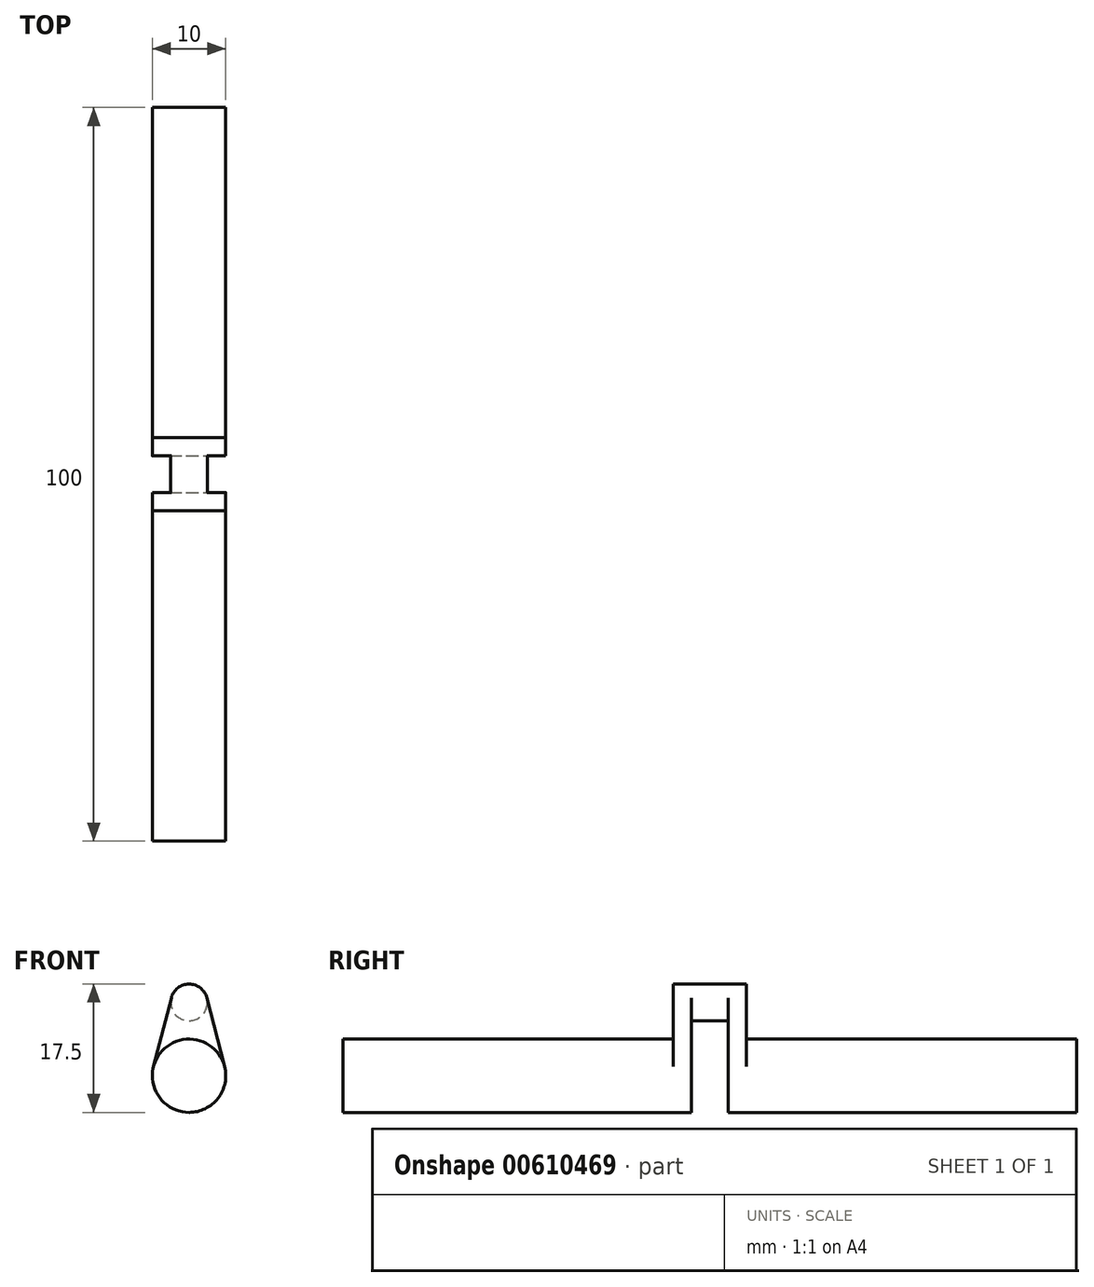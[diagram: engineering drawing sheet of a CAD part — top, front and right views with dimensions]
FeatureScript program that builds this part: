
annotation { "Feature Type Name" : "Feature", "Feature Type Description" : "" }
export const myFeature = defineFeature(function(context is Context, id is Id, definition is map)
    precondition{}
    {
        {
            var Q0;
            Q0=qCreatedBy(makeId("Front.planeOp"),FACE);
            var sketch = newSketch(context, id + "F0", { "sketchPlane" : qUnion([Q0])});
            skCircle(sketch, "E0", {"center": v(0, 0) * mm, "radius": 5 * mm});
            skLineSegment(sketch, "E1", {"start": v(4.84, 1.25) * mm, "end": v(2.42, 10.62) * mm});
            skLineSegment(sketch, "E2", {"start": v(-4.84, 1.25) * mm, "end": v(-2.42, 10.63) * mm});
            skCircle(sketch, "E3", {"center": v(0, 10) * mm, "radius": 2.5 * mm});
            skSolve(sketch);
        }
        {
            var Q0;
            {var subQ0=sQuery(id+"F0.wireOp",EDGE,"E3");var subQ1=makeQuery(id+"F0.imprint","INTERSECT",VERTEX,{"derivedFrom":[sQuery(id+"F0.wireOp",EDGE,"E1"),subQ0]});Q0=makeQuery(id+"F0.imprint","IMPRINT",FACE,{"disambiguationData":[TD([[makeQuery(id+"F0.imprint","IMPRINT",EDGE,{"disambiguationData":[TD([[subQ1,-1.0]])],"derivedFrom":subQ0}),1.0]])]});}
            var Q1;
            {var subQ0=sQuery(id+"F0.wireOp",EDGE,"E1");Q1=makeQuery(id+"F0.imprint","IMPRINT",FACE,{"disambiguationData":[TD([[makeQuery(id+"F0.imprint","IMPRINT",EDGE,{"derivedFrom":subQ0}),1.0]])]});}
            var Q2;
            {var subQ0=sQuery(id+"F0.wireOp",EDGE,"E0");var subQ1=makeQuery(id+"F0.imprint","INTERSECT",VERTEX,{"derivedFrom":[subQ0,sQuery(id+"F0.wireOp",EDGE,"E1")]});Q2=makeQuery(id+"F0.imprint","IMPRINT",FACE,{"disambiguationData":[TD([[makeQuery(id+"F0.imprint","IMPRINT",EDGE,{"disambiguationData":[TD([[subQ1,-1.0]])],"derivedFrom":subQ0}),1.0]])]});}
            extrude(context, id + "F1", {"entities" : qUnion([Q0, Q1, Q2]), "endBound" : BoundingType.SYMMETRIC, "depth" : 10 * mm, "offsetDistance" : 25 * mm});
        }
        {
            var Q0;
            {var subQ0=sQuery(id+"F0.wireOp",EDGE,"E0");var subQ1=makeQuery(id+"F0.imprint","INTERSECT",VERTEX,{"derivedFrom":[subQ0,sQuery(id+"F0.wireOp",EDGE,"E1")]});Q0=makeQuery(id+"F0.imprint","IMPRINT",FACE,{"disambiguationData":[TD([[makeQuery(id+"F0.imprint","IMPRINT",EDGE,{"disambiguationData":[TD([[subQ1,-1.0]])],"derivedFrom":subQ0}),1.0]])]});}
            extrude(context, id + "F2", {"entities" : qUnion([Q0]), "operationType" : NewBodyOperationType.ADD, "endBound" : BoundingType.SYMMETRIC, "depth" : 100 * mm, "offsetDistance" : 25 * mm});
        }
        {
            var Q0;
            {var subQ0=sQuery(id+"F0.wireOp",EDGE,"E1");Q0=makeQuery(id+"F0.imprint","IMPRINT",FACE,{"disambiguationData":[TD([[makeQuery(id+"F0.imprint","IMPRINT",EDGE,{"derivedFrom":subQ0}),1.0]])]});}
            var Q1;
            {var subQ0=sQuery(id+"F0.wireOp",EDGE,"E0");var subQ1=makeQuery(id+"F0.imprint","INTERSECT",VERTEX,{"derivedFrom":[subQ0,sQuery(id+"F0.wireOp",EDGE,"E1")]});Q1=makeQuery(id+"F0.imprint","IMPRINT",FACE,{"disambiguationData":[TD([[makeQuery(id+"F0.imprint","IMPRINT",EDGE,{"disambiguationData":[TD([[subQ1,-1.0]])],"derivedFrom":subQ0}),1.0]])]});}
            extrude(context, id + "F3", {"entities" : qUnion([Q0, Q1]), "operationType" : NewBodyOperationType.REMOVE, "endBound" : BoundingType.SYMMETRIC, "oppositeDirection" : true, "depth" : 5 * mm, "offsetDistance" : 25 * mm});
        }
    });
